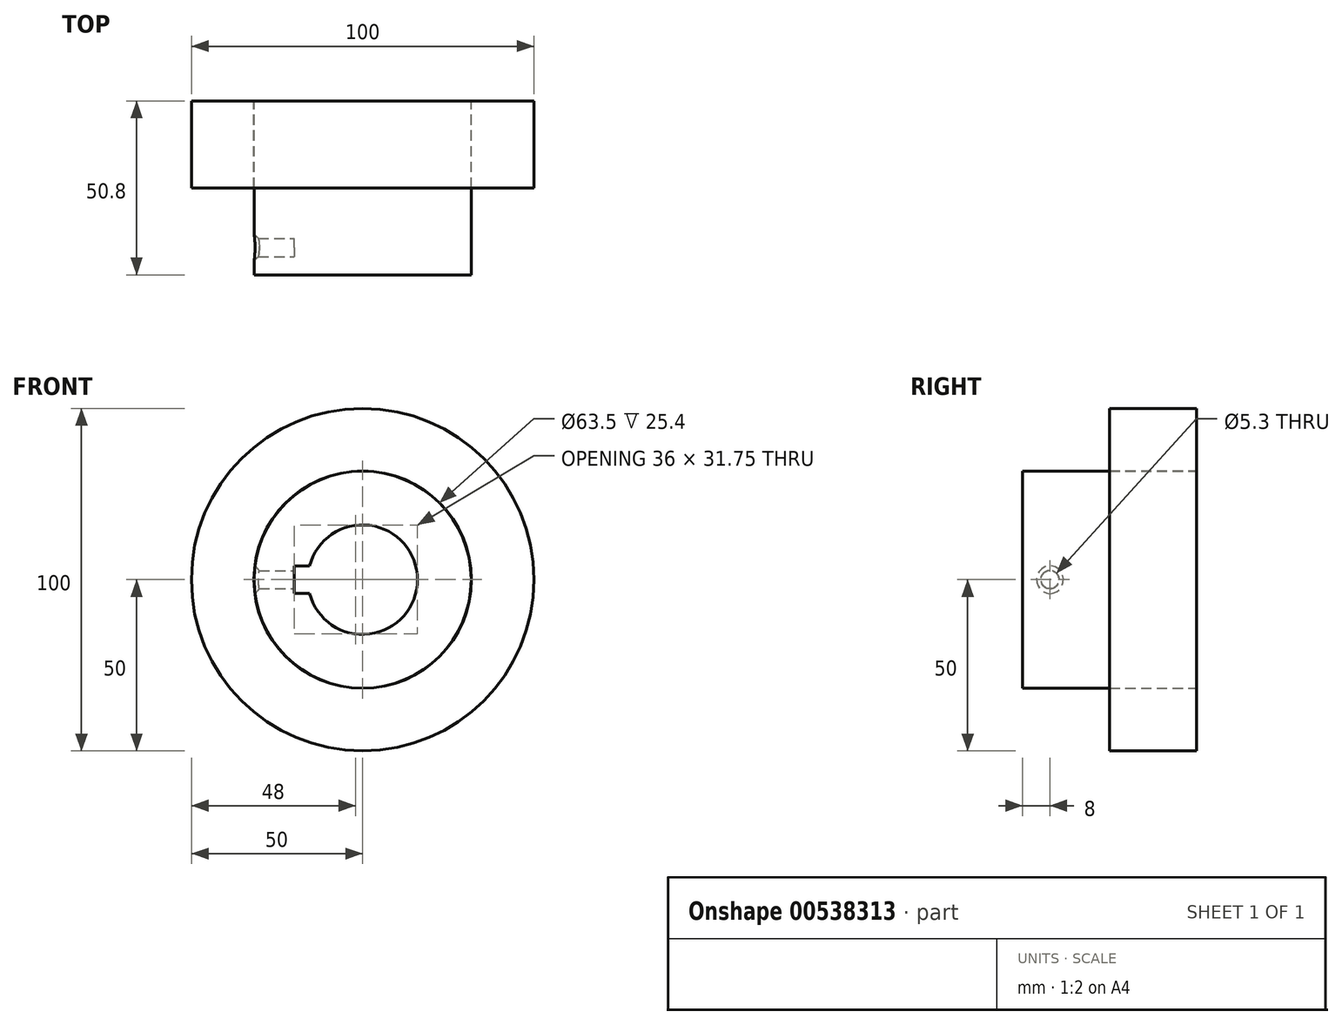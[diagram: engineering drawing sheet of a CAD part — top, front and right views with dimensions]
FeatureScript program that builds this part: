
annotation { "Feature Type Name" : "Feature", "Feature Type Description" : "" }
export const myFeature = defineFeature(function(context is Context, id is Id, definition is map)
    precondition{}
    {
        {
            var Q0;
            Q0=qCreatedBy(makeId("Front.planeOp"),FACE);
            var sketch = newSketch(context, id + "F0", { "sketchPlane" : qUnion([Q0])});
            skCircle(sketch, "E0", {"center": v(0, 0) * mm, "radius": 50 * mm});
            skCircle(sketch, "E1", {"center": v(0, 0) * mm, "radius": 31.75 * mm});
            skSolve(sketch);
        }
        {
            var Q0;
            Q0=makeQuery(id+"F0.imprint","IMPRINT",FACE,{"disambiguationData":[TD([[makeQuery(id+"F0.imprint","IMPRINT",EDGE,{"derivedFrom":sQuery(id+"F0.wireOp",EDGE,"E0")}),1.0]])]});
            extrude(context, id + "F1", {"entities" : qUnion([Q0]), "depth" : 25.4 * mm, "offsetDistance" : 25.4 * mm});
        }
        {
            var Q0;
            Q0=qCreatedBy(makeId("Front.planeOp"),FACE);
            var sketch = newSketch(context, id + "F2", { "sketchPlane" : qUnion([Q0])});
            skCircle(sketch, "E2", {"center": v(0, 0) * mm, "radius": 31.68 * mm});
            skSolve(sketch);
        }
        {
            var Q0;
            Q0 = qSketchRegion(id + "F2", true);
            extrude(context, id + "F3", {"entities" : qUnion([Q0]), "depth" : 25.4 * mm, "offsetDistance" : 25.4 * mm});
        }
        {
            var Q0;
            Q0=qCreatedBy(makeId("Front.planeOp"),FACE);
            var sketch = newSketch(context, id + "F4", { "sketchPlane" : qUnion([Q0])});
            skCircle(sketch, "E3", {"center": v(0, 0) * mm, "radius": 16 * mm});
            skSolve(sketch);
        }
        {
            var Q0;
            Q0 = qSketchRegion(id + "F4", true);
            extrude(context, id + "F5", {"entities" : qUnion([Q0]), "operationType" : NewBodyOperationType.REMOVE, "endBound" : BoundingType.THROUGH_ALL, "oppositeDirection" : true, "depth" : 25.4 * mm, "offsetDistance" : 25.4 * mm});
        }
        {
            var Q0;
            Q0=makeQuery(id+"F3.opExtrude","CAP_FACE",FACE,{"disambiguationData":[OSD([sQuery(id+"F2.wireOp",EDGE,"E2")])],"isStart":false});
            var sketch = newSketch(context, id + "F6", { "sketchPlane" : qUnion([Q0])});
            skCircle(sketch, "E4", {"center": v(0, 0) * mm, "radius": 16 * mm});
            skSolve(sketch);
        }
        {
            var Q0;
            Q0 = qSketchRegion(id + "F6", true);
            extrude(context, id + "F7", {"entities" : qUnion([Q0]), "operationType" : NewBodyOperationType.REMOVE, "endBound" : BoundingType.THROUGH_ALL, "oppositeDirection" : true, "depth" : 25.4 * mm, "offsetDistance" : 25.4 * mm});
        }
        {
            var Q0;
            Q0=makeQuery(id+"F3.opExtrude","CAP_FACE",FACE,{"disambiguationData":[OSD([sQuery(id+"F2.wireOp",EDGE,"E2")])],"isStart":false});
            extrude(context, id + "F8", {"entities" : qUnion([Q0]), "operationType" : NewBodyOperationType.ADD, "depth" : 25.4 * mm, "offsetDistance" : 25.4 * mm});
        }
        {
            var Q0;
            Q0=qCreatedBy(makeId("Right.planeOp"),FACE);
            var sketch = newSketch(context, id + "F9", { "sketchPlane" : qUnion([Q0])});
            skCircle(sketch, "E5", {"center": v(-42.8, 0) * mm, "radius": 2.65 * mm});
            skSolve(sketch);
        }
        {
            var Q0;
            Q0 = qSketchRegion(id + "F9", true);
            extrude(context, id + "F10", {"entities" : qUnion([Q0]), "operationType" : NewBodyOperationType.REMOVE, "oppositeDirection" : true, "depth" : 50.8 * mm, "offsetDistance" : 25.4 * mm});
        }
        {
            var Q0;
            {var subQ0=sQuery(id+"F2.wireOp",EDGE,"E2");Q0=makeQuery(id+"F10.boolean.opBoolean","INTERSECT",EDGE,{"derivedFrom":[makeQuery(id+"F8.boolean.opBoolean","MERGE",FACE,{"derivedFrom":[makeQuery(id+"F3.opExtrude","SWEPT_FACE",FACE,{"disambiguationData":[OSD([subQ0])]}),makeQuery(id+"F8.opExtrude","SWEPT_FACE",FACE,{"disambiguationData":[OSD([subQ0])]})]}),makeQuery(id+"F10.opExtrude","SWEPT_FACE",FACE,{"disambiguationData":[OSD([sQuery(id+"F9.wireOp",EDGE,"E5")])]})]});}
            chamfer(context, id + "F11", {"entities" : qUnion([Q0]), "width" : 1.27 * mm, "tangentPropagation" : true});
        }
        {
            var Q0;
            Q0=makeQuery(id+"F8.opExtrude","CAP_FACE",FACE,{"disambiguationData":[OSD([sQuery(id+"F2.wireOp",EDGE,"E2")])],"isStart":false});
            var sketch = newSketch(context, id + "F12", { "sketchPlane" : qUnion([Q0])});
            skLineSegment(sketch, "E6.bottom", {"start": v(-12, 4) * mm, "end": v(-20, 4) * mm});
            skLineSegment(sketch, "E6.top", {"start": v(-12, -4) * mm, "end": v(-20, -4) * mm});
            skLineSegment(sketch, "E6.left", {"start": v(-12, 4) * mm, "end": v(-12, -4) * mm});
            skLineSegment(sketch, "E6.right", {"start": v(-20, 4) * mm, "end": v(-20, -4) * mm});
            skPoint(sketch, "E6.middle", {"position": v(-16, 0) * mm});
            skSolve(sketch);
        }
        {
            var Q0;
            Q0 = qSketchRegion(id + "F12", true);
            extrude(context, id + "F13", {"entities" : qUnion([Q0]), "operationType" : NewBodyOperationType.REMOVE, "endBound" : BoundingType.THROUGH_ALL, "oppositeDirection" : true, "depth" : 25.4 * mm, "offsetDistance" : 25.4 * mm});
        }
    });
